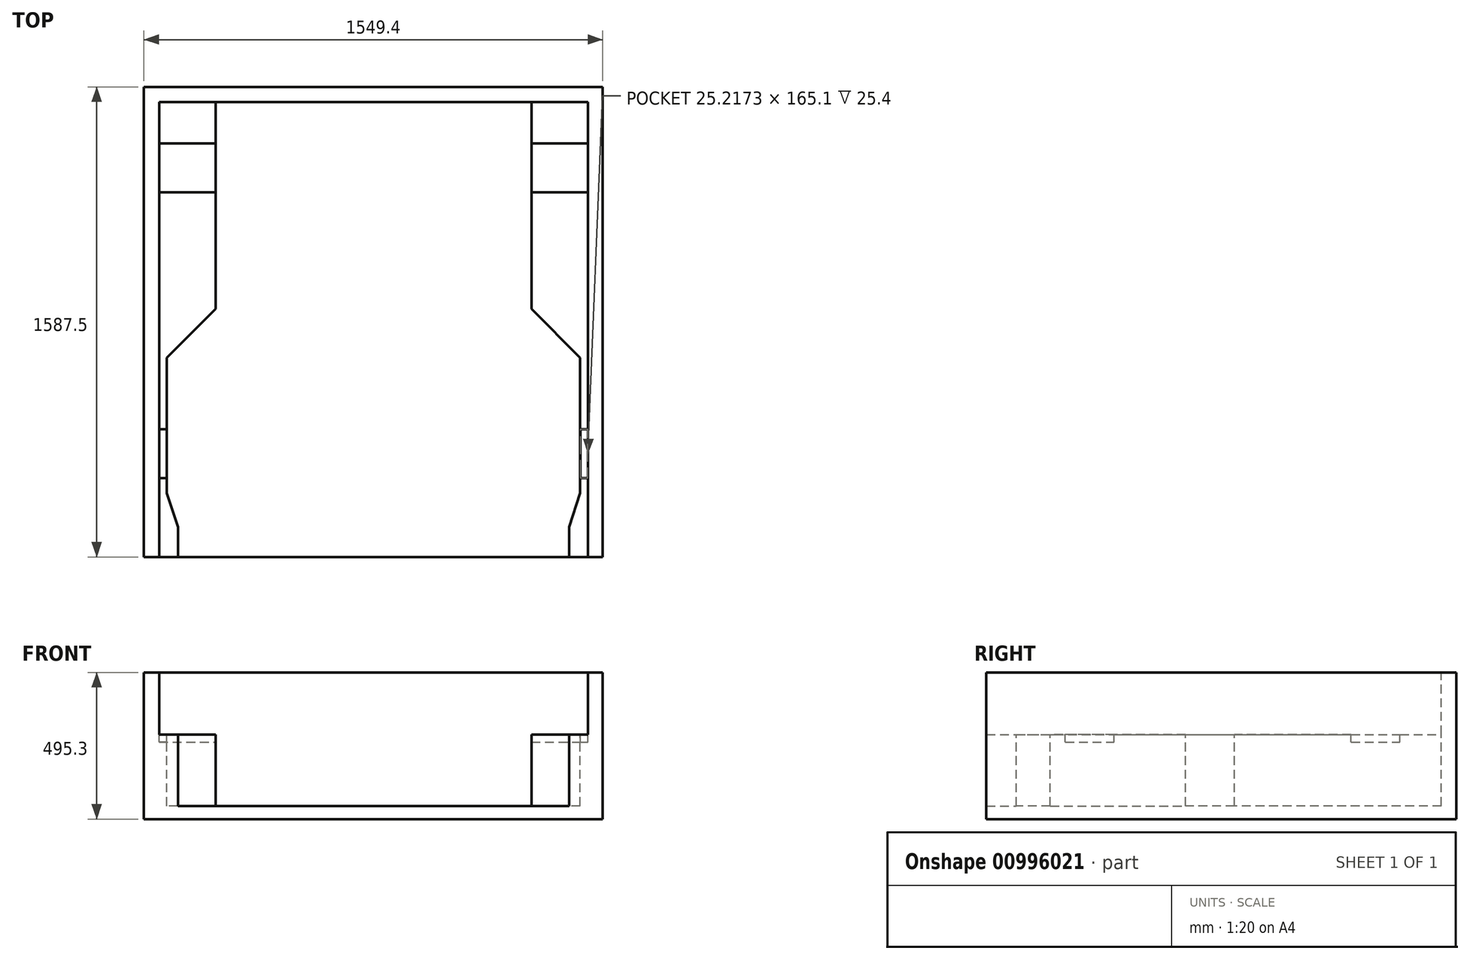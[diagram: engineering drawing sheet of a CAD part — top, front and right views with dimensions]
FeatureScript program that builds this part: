
annotation { "Feature Type Name" : "Feature", "Feature Type Description" : "" }
export const myFeature = defineFeature(function(context is Context, id is Id, definition is map)
    precondition{}
    {
        {
            var Q0;
            Q0=qCreatedBy(makeId("Top.planeOp"),FACE);
            var sketch = newSketch(context, id + "F0", { "sketchPlane" : qUnion([Q0])});
            skLineSegment(sketch, "E0.bottom", {"start": v(0, 0) * mm, "end": v(1549.4, 0) * mm});
            skLineSegment(sketch, "E0.top", {"start": v(0, 1587.5) * mm, "end": v(1549.4, 1587.5) * mm});
            skLineSegment(sketch, "E0.left", {"start": v(0, 0) * mm, "end": v(0, 1587.5) * mm});
            skLineSegment(sketch, "E0.right", {"start": v(1549.4, 0) * mm, "end": v(1549.4, 1587.5) * mm});
            skSolve(sketch);
        }
        {
            var Q0;
            Q0 = qSketchRegion(id + "F0", true);
            extrude(context, id + "F1", {"entities" : qUnion([Q0]), "depth" : 495.3 * mm, "offsetDistance" : 25.4 * mm});
        }
        {
            var Q0;
            Q0=makeQuery(id+"F1.opExtrude","CAP_FACE",FACE,{"disambiguationData":[OSD([sQuery(id+"F0.wireOp",EDGE,"E0.bottom"),sQuery(id+"F0.wireOp",EDGE,"E0.top"),sQuery(id+"F0.wireOp",EDGE,"E0.left"),sQuery(id+"F0.wireOp",EDGE,"E0.right")])],"isStart":false});
            var sketch = newSketch(context, id + "F2", { "sketchPlane" : qUnion([Q0])});
            skLineSegment(sketch, "E1.bottom", {"start": v(50.8, 0) * mm, "end": v(1498.6, 0) * mm});
            skLineSegment(sketch, "E1.top", {"start": v(50.8, 1536.7) * mm, "end": v(1498.6, 1536.7) * mm});
            skLineSegment(sketch, "E1.left", {"start": v(50.8, 0) * mm, "end": v(50.8, 1536.7) * mm});
            skLineSegment(sketch, "E1.right", {"start": v(1498.6, 0) * mm, "end": v(1498.6, 1536.7) * mm});
            skSolve(sketch);
        }
        {
            var Q0;
            Q0 = qSketchRegion(id + "F2", true);
            extrude(context, id + "F3", {"entities" : qUnion([Q0]), "operationType" : NewBodyOperationType.REMOVE, "oppositeDirection" : true, "depth" : 209.55 * mm, "offsetDistance" : 25.4 * mm});
        }
        {
            var Q0;
            Q0=makeQuery(id+"F3.boolean.opBoolean","COPY",FACE,{"derivedFrom":makeQuery(id+"F3.opExtrude","CAP_FACE",FACE,{"disambiguationData":[OSD([sQuery(id+"F2.wireOp",EDGE,"E1.bottom"),sQuery(id+"F2.wireOp",EDGE,"E1.top"),sQuery(id+"F2.wireOp",EDGE,"E1.left"),sQuery(id+"F2.wireOp",EDGE,"E1.right")])],"isStart":false})});
            var sketch = newSketch(context, id + "F4", { "sketchPlane" : qUnion([Q0])});
            skLineSegment(sketch, "E2", {"start": v(114.3, 0) * mm, "end": v(114.3, 101.6) * mm});
            skLineSegment(sketch, "E3", {"start": v(114.3, 101.6) * mm, "end": v(76.2, 215.9) * mm});
            skLineSegment(sketch, "E4", {"start": v(76.2, 215.9) * mm, "end": v(76.2, 673.1) * mm});
            skLineSegment(sketch, "E5", {"start": v(76.2, 673.1) * mm, "end": v(241.3, 673.1) * mm});
            skLineSegment(sketch, "E6", {"start": v(241.3, 673.1) * mm, "end": v(241.3, 1536.7) * mm});
            skLineSegment(sketch, "E7", {"start": v(241.3, 1536.7) * mm, "end": v(1308.1, 1536.7) * mm});
            skLineSegment(sketch, "E8", {"start": v(1308.1, 1536.7) * mm, "end": v(1308.1, 673.1) * mm});
            skLineSegment(sketch, "E9", {"start": v(1308.1, 673.1) * mm, "end": v(1473.2, 673.1) * mm});
            skLineSegment(sketch, "E10", {"start": v(1473.2, 673.1) * mm, "end": v(1473.2, 215.9) * mm});
            skLineSegment(sketch, "E11", {"start": v(1473.2, 215.9) * mm, "end": v(1435.1, 101.6) * mm});
            skLineSegment(sketch, "E12", {"start": v(1435.1, 101.6) * mm, "end": v(1435.1, 0) * mm});
            skLineSegment(sketch, "E13", {"start": v(1435.1, 0) * mm, "end": v(114.3, 0) * mm});
            skSolve(sketch);
        }
        {
            var Q0;
            Q0=makeQuery(id+"F4.imprint","IMPRINT",FACE,{"disambiguationData":[TD([[makeQuery(id+"F4.imprint","IMPRINT",EDGE,{"derivedFrom":sQuery(id+"F4.wireOp",EDGE,"E2")}),-1.0]])]});
            extrude(context, id + "F5", {"entities" : qUnion([Q0]), "operationType" : NewBodyOperationType.REMOVE, "oppositeDirection" : true, "depth" : 241.3 * mm, "offsetDistance" : 25.4 * mm});
        }
        {
            var Q0;
            Q0=makeQuery(id+"F5.boolean.opBoolean","COPY",EDGE,{"derivedFrom":makeQuery(id+"F5.opExtrude","SWEPT_EDGE",EDGE,{"disambiguationData":[OSD([sQuery(id+"F4.wireOp",EDGE,"E5"),sQuery(id+"F4.wireOp",EDGE,"E6")])]})});
            chamfer(context, id + "F6", {"entities" : qUnion([Q0]), "width" : 165.1 * mm, "tangentPropagation" : true});
        }
        {
            var Q0;
            Q0=makeQuery(id+"F5.boolean.opBoolean","COPY",EDGE,{"derivedFrom":makeQuery(id+"F5.opExtrude","SWEPT_EDGE",EDGE,{"disambiguationData":[OSD([sQuery(id+"F4.wireOp",EDGE,"E8"),sQuery(id+"F4.wireOp",EDGE,"E9")])]})});
            chamfer(context, id + "F7", {"entities" : qUnion([Q0]), "width" : 165.1 * mm, "tangentPropagation" : true});
        }
        {
            var Q0;
            {var subQ0=sQuery(id+"F2.wireOp",EDGE,"E1.top");var subQ1=sQuery(id+"F2.wireOp",EDGE,"E1.left");Q0=makeQuery(id+"F5.boolean.opBoolean","SPLIT",FACE,{"disambiguationData":[TD([makeQuery(id+"F3.boolean.opBoolean","COPY",FACE,{"derivedFrom":makeQuery(id+"F3.opExtrude","SWEPT_FACE",FACE,{"disambiguationData":[OSD([subQ1])]})})])],"derivedFrom":makeQuery(id+"F3.boolean.opBoolean","COPY",FACE,{"derivedFrom":makeQuery(id+"F3.opExtrude","CAP_FACE",FACE,{"disambiguationData":[OSD([sQuery(id+"F2.wireOp",EDGE,"E1.bottom"),subQ0,subQ1,sQuery(id+"F2.wireOp",EDGE,"E1.right")])],"isStart":false})})});}
            var sketch = newSketch(context, id + "F8", { "sketchPlane" : qUnion([Q0])});
            skLineSegment(sketch, "E14.bottom", {"start": v(1307.45, 1397) * mm, "end": v(1499.54, 1397) * mm});
            skLineSegment(sketch, "E14.top", {"start": v(1307.45, 1231.9) * mm, "end": v(1499.54, 1231.9) * mm});
            skLineSegment(sketch, "E14.left", {"start": v(1307.45, 1397) * mm, "end": v(1307.45, 1231.9) * mm});
            skLineSegment(sketch, "E14.right", {"start": v(1499.54, 1397) * mm, "end": v(1499.54, 1231.9) * mm});
            skLineSegment(sketch, "E15.bottom", {"start": v(76.2, 431.8) * mm, "end": v(50.8, 431.8) * mm});
            skLineSegment(sketch, "E15.top", {"start": v(76.2, 266.7) * mm, "end": v(50.8, 266.7) * mm});
            skLineSegment(sketch, "E15.left", {"start": v(76.2, 431.8) * mm, "end": v(76.2, 266.7) * mm});
            skLineSegment(sketch, "E15.right", {"start": v(50.8, 431.8) * mm, "end": v(50.8, 266.7) * mm});
            skLineSegment(sketch, "E16.bottom", {"start": v(1473.33, 431.8) * mm, "end": v(1498.55, 431.8) * mm});
            skLineSegment(sketch, "E16.top", {"start": v(1473.33, 266.7) * mm, "end": v(1498.55, 266.7) * mm});
            skLineSegment(sketch, "E16.left", {"start": v(1473.33, 431.8) * mm, "end": v(1473.33, 266.7) * mm});
            skLineSegment(sketch, "E16.right", {"start": v(1498.55, 431.8) * mm, "end": v(1498.55, 266.7) * mm});
            skLineSegment(sketch, "E17.bottom", {"start": v(50.8, 1397) * mm, "end": v(241.3, 1397) * mm});
            skLineSegment(sketch, "E17.top", {"start": v(50.8, 1231.9) * mm, "end": v(241.3, 1231.9) * mm});
            skLineSegment(sketch, "E17.left", {"start": v(50.8, 1397) * mm, "end": v(50.8, 1231.9) * mm});
            skLineSegment(sketch, "E17.right", {"start": v(241.3, 1397) * mm, "end": v(241.3, 1231.9) * mm});
            skSolve(sketch);
        }
        {
            var Q0;
            Q0 = qSketchRegion(id + "F8", true);
            extrude(context, id + "F9", {"entities" : qUnion([Q0]), "operationType" : NewBodyOperationType.REMOVE, "oppositeDirection" : true, "depth" : 25.4 * mm, "offsetDistance" : 25.4 * mm});
        }
    });
